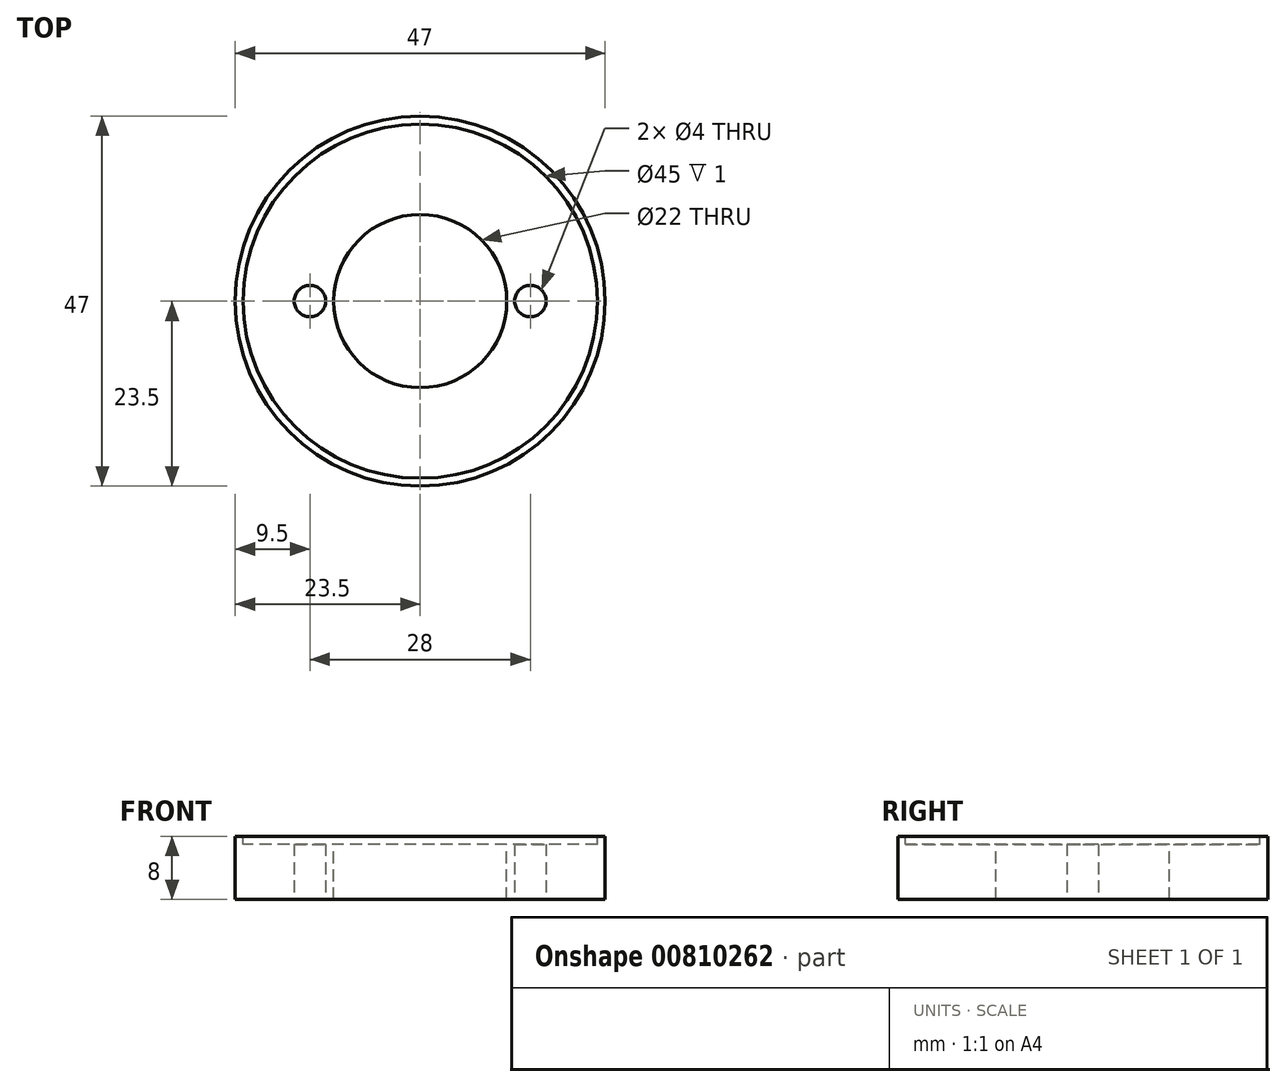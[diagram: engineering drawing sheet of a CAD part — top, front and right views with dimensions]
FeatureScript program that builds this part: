
annotation { "Feature Type Name" : "Feature", "Feature Type Description" : "" }
export const myFeature = defineFeature(function(context is Context, id is Id, definition is map)
    precondition{}
    {
        {
            var Q0;
            Q0=qCreatedBy(makeId("Front.planeOp"),FACE);
            var sketch = newSketch(context, id + "F0", { "sketchPlane" : qUnion([Q0])});
            skLineSegment(sketch, "E0", {"start": v(0, 20.62) * mm, "end": v(-23.5, 20.62) * mm});
            skLineSegment(sketch, "E1", {"start": v(-23.5, 20.62) * mm, "end": v(-23.5, 28.62) * mm});
            skLineSegment(sketch, "E2", {"start": v(-23.5, 28.62) * mm, "end": v(-22.5, 28.62) * mm});
            skLineSegment(sketch, "E3", {"start": v(-22.5, 28.62) * mm, "end": v(-22.5, 27.62) * mm});
            skLineSegment(sketch, "E4", {"start": v(-22.5, 27.62) * mm, "end": v(0, 27.62) * mm});
            skLineSegment(sketch, "E5", {"start": v(-11, 20.62) * mm, "end": v(-11, 27.62) * mm});
            skLineSegment(sketch, "E6", {"start": v(0, 27.62) * mm, "end": v(0, 20.62) * mm});
            skSolve(sketch);
        }
        {
            var Q0;
            {var subQ1=sQuery(id+"F0.wireOp",EDGE,"E1");Q0=makeQuery(id+"F0.imprint","IMPRINT",FACE,{"disambiguationData":[TD([[makeQuery(id+"F0.imprint","IMPRINT",EDGE,{"derivedFrom":subQ1}),-1.0]])]});}
            var Q1;
            Q1=sQuery(id+"F0.wireOp",EDGE,"E6");
            revolve(context, id + "F1", {"entities" : qUnion([Q0]), "axis" : qUnion([Q1]), "revolveType" : RevolveType.FULL, "surfaceOperationType" : NewSurfaceOperationType.NEW});
        }
        {
            var Q0;
            Q0=makeQuery(id+"F1.opRevolve","SWEPT_FACE",FACE,{"disambiguationData":[OSD([sQuery(id+"F0.wireOp",EDGE,"E0")])]});
            var sketch = newSketch(context, id + "F2", { "sketchPlane" : qUnion([Q0])});
            skPoint(sketch, "E7", {"position": v(-14, 0) * mm});
            skPoint(sketch, "E8.1.0", {"position": v(14, 0) * mm});
            skPoint(sketch, "E8.center", {"position": v(0, 0) * mm});
            skSolve(sketch);
        }
        {
            var Q0;
            Q0=sQuery(id+"F2.wireOp",VERTEX,"E7");
            var Q1;
            Q1=sQuery(id+"F2.wireOp",VERTEX,"E8.1.0");
            var Q2;
            Q2=makeQuery(id+"F1.opRevolve","SWEPT_BODY",BODY,{"disambiguationData":[OSD([sQuery(id+"F0.wireOp",EDGE,"E0"),sQuery(id+"F0.wireOp",EDGE,"jssrVroJ-Oz3R-KxdV-gQoA-S6XikDruUh1q"),sQuery(id+"F0.wireOp",EDGE,"I1IZs9et-yzp2-pkoH-Uqyj-Zst5VyObDKE9"),sQuery(id+"F0.wireOp",EDGE,"TEGZxwhD-VCsi-AP2g-Tj0f-wSHnz4qmJ26e"),sQuery(id+"F0.wireOp",EDGE,"TgjRPXJ9-tEQl-qVCL-aCPt-cUJG5a0YcU9j"),sQuery(id+"F0.wireOp",EDGE,"GWbyFsqO-qvGy-h0sl-CkvS-dSc1ia9C2u4k")])]});
            hole(context, id + "F3", {"style" : HoleStyle.SIMPLE, "endStyle" : HoleEndStyle.THROUGH, "holeDiameter" : 4 * mm, "isTappedThrough" : true, "tappedDepth" : 12 * mm, "tapClearance" : 3, "locations" : qUnion([Q0, Q1]), "scope" : qUnion([Q2]), "majorDiameter" : 5 * mm});
        }
    });
